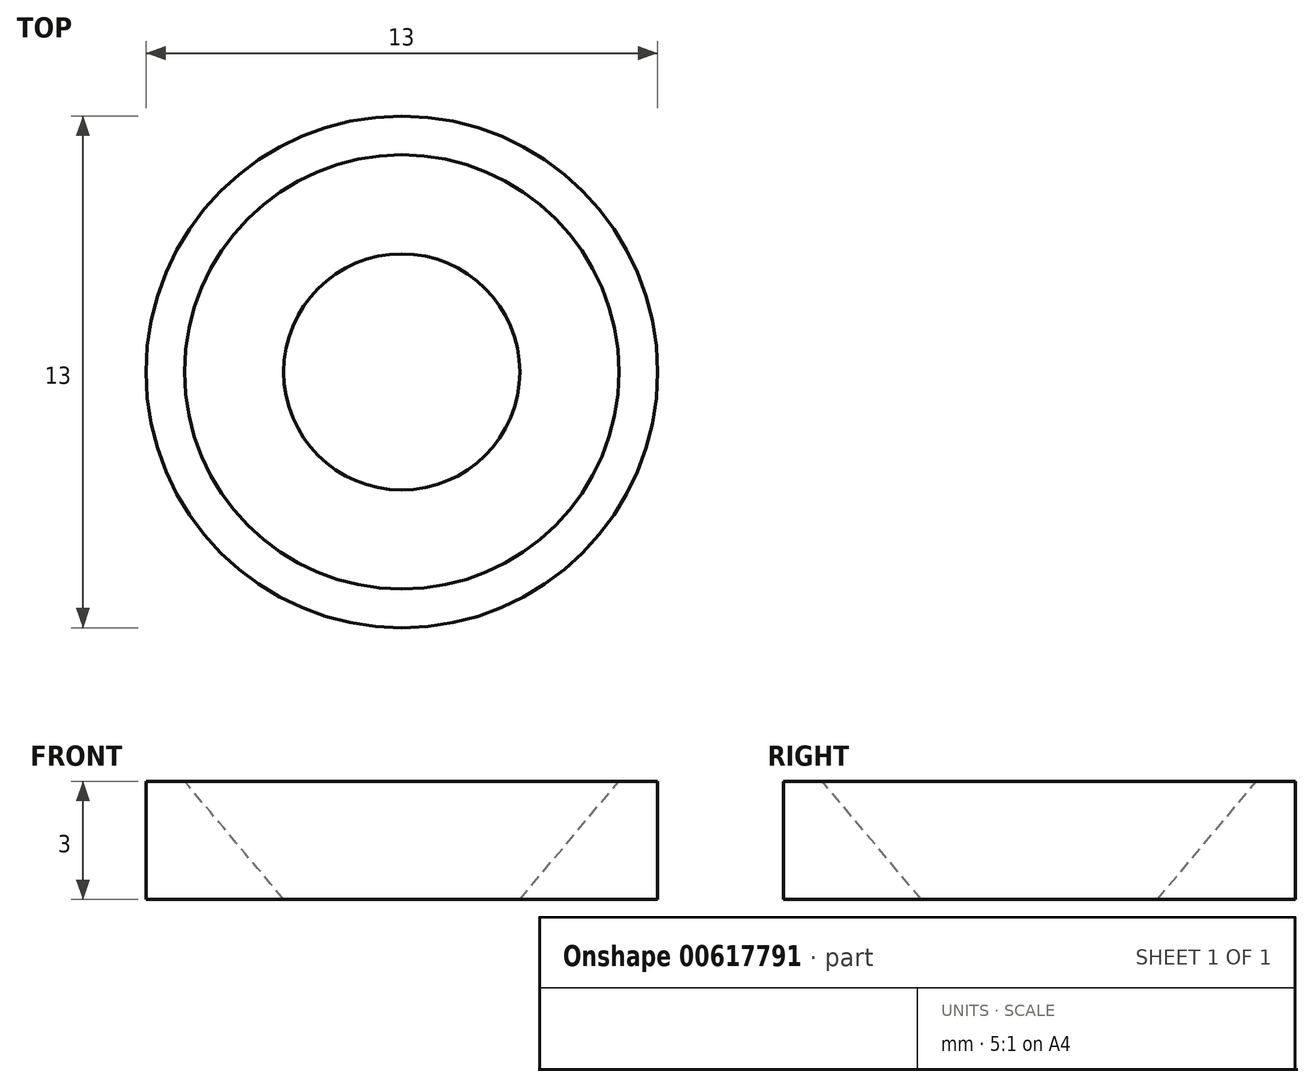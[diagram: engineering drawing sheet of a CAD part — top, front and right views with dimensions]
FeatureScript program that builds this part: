
annotation { "Feature Type Name" : "Feature", "Feature Type Description" : "" }
export const myFeature = defineFeature(function(context is Context, id is Id, definition is map)
    precondition{}
    {
        {
            var Q0;
            Q0=qCreatedBy(makeId("Front.planeOp"),FACE);
            var sketch = newSketch(context, id + "F0", { "sketchPlane" : qUnion([Q0])});
            skLineSegment(sketch, "E0", {"start": v(0, 0) * mm, "end": v(0, 3) * mm, "construction": true});
            skLineSegment(sketch, "E1", {"start": v(6.5, 0) * mm, "end": v(6.5, 3) * mm});
            skLineSegment(sketch, "E2", {"start": v(6.5, 3) * mm, "end": v(5.52, 3) * mm});
            skLineSegment(sketch, "E3", {"start": v(5.52, 3) * mm, "end": v(3, 0) * mm});
            skLineSegment(sketch, "E4", {"start": v(3, 0) * mm, "end": v(6.5, 0) * mm});
            skSolve(sketch);
        }
        {
            var Q0;
            Q0=makeQuery(id+"F0.imprint","IMPRINT",FACE,{"disambiguationData":[TD([[makeQuery(id+"F0.imprint","IMPRINT",EDGE,{"derivedFrom":sQuery(id+"F0.wireOp",EDGE,"E1")}),1.0]])]});
            var Q1;
            Q1=sQuery(id+"F0.wireOp",EDGE,"E0");
            revolve(context, id + "F1", {"entities" : qUnion([Q0]), "axis" : qUnion([Q1]), "revolveType" : RevolveType.FULL});
        }
    });
